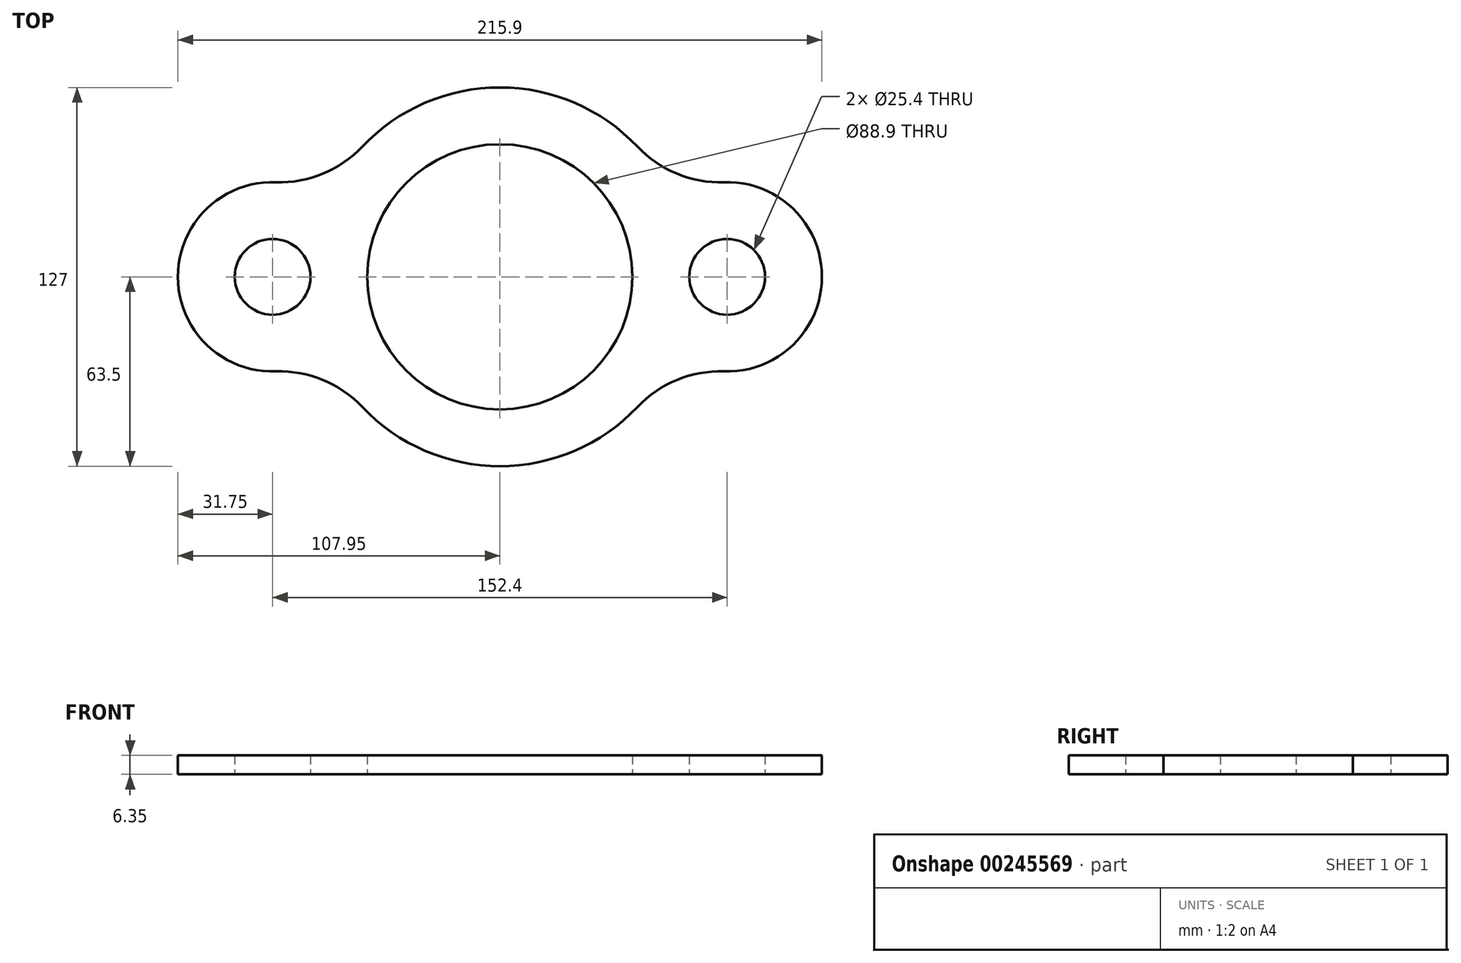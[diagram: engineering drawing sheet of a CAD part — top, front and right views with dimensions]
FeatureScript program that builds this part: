
annotation { "Feature Type Name" : "Feature", "Feature Type Description" : "" }
export const myFeature = defineFeature(function(context is Context, id is Id, definition is map)
    precondition{}
    {
        {
            var Q0;
            Q0=qCreatedBy(makeId("Top.planeOp"),FACE);
            var sketch = newSketch(context, id + "F0", { "sketchPlane" : qUnion([Q0])});
            skArc(sketch, "E0", {"start": v(-46.14, -43.63) * mm, "mid": v(0, -63.5) * mm, "end": v(46.14, -43.63) * mm});
            skCircle(sketch, "E1", {"center": v(0, 0) * mm, "radius": 44.45 * mm});
            skArc(sketch, "E2", {"start": v(75.12, -31.73) * mm, "mid": v(107.95, 0) * mm, "end": v(75.12, 31.73) * mm});
            skCircle(sketch, "E3", {"center": v(76.2, 0) * mm, "radius": 12.7 * mm});
            skArc(sketch, "E4", {"start": v(-75.12, 31.73) * mm, "mid": v(-107.95, 0) * mm, "end": v(-75.12, -31.73) * mm});
            skCircle(sketch, "E5", {"center": v(-76.2, 0) * mm, "radius": 12.7 * mm});
            skArc(sketch, "E6.trimOffspring", {"start": v(46.14, 43.63) * mm, "mid": v(0, 63.5) * mm, "end": v(-46.14, 43.63) * mm});
            skPoint(sketch, "E7.visualSharp", {"position": v(-57.94, 25.98) * mm});
            skArc(sketch, "E7.filletArc", {"start": v(-75.12, 31.73) * mm, "mid": v(-59.35, 34.56) * mm, "end": v(-46.14, 43.63) * mm});
            skPoint(sketch, "E8.visualSharp", {"position": v(-57.94, -25.98) * mm});
            skArc(sketch, "E8.filletArc", {"start": v(-46.14, -43.63) * mm, "mid": v(-59.35, -34.56) * mm, "end": v(-75.12, -31.73) * mm});
            skPoint(sketch, "E9.visualSharp", {"position": v(57.94, -25.98) * mm});
            skArc(sketch, "E9.filletArc", {"start": v(75.12, -31.73) * mm, "mid": v(59.35, -34.56) * mm, "end": v(46.14, -43.63) * mm});
            skPoint(sketch, "E10.visualSharp", {"position": v(57.94, 25.98) * mm});
            skArc(sketch, "E10.filletArc", {"start": v(46.14, 43.63) * mm, "mid": v(59.35, 34.56) * mm, "end": v(75.12, 31.73) * mm});
            skSolve(sketch);
        }
        {
            var Q0;
            Q0=makeQuery(id+"F0.imprint","IMPRINT",FACE,{"disambiguationData":[TD([[makeQuery(id+"F0.imprint","IMPRINT",EDGE,{"derivedFrom":sQuery(id+"F0.wireOp",EDGE,"E0")}),1.0]])]});
            extrude(context, id + "F1", {"entities" : qUnion([Q0]), "depth" : 6.35 * mm});
        }
    });
